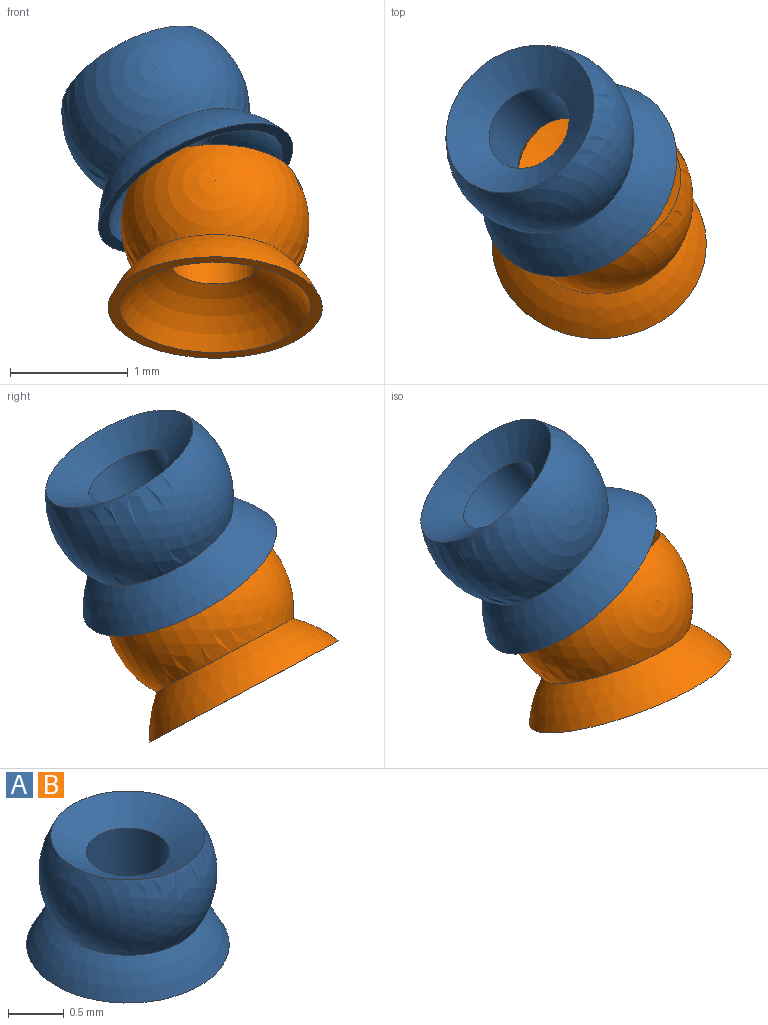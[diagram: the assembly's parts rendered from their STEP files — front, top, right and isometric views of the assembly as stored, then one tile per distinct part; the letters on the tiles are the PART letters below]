
ASSEMBLY  parts=2 mates=1
PART A: 6 faces, bbox 1.8x1.8x1.6 mm
  f0: sphere r=0.9mm, area 2.4mm2, adj f3,f4
  f1: sphere r=0.8mm, area 4.3mm2, adj f2,f5
  f2: sphere r=0.99mm, area 2.2mm2, adj f1,f3
  f3: plane 1.82x1.82mm, normal (0,0,-1), area 0.5mm2, adj f0,f2
  f4: cylinder r=0.38mm len=0.75mm, axis (0,0,-1), area 1.4mm2, adj f0,f5
  f5: cone r=0mm half-angle=60deg, axis (0,0,1), area 1.2mm2, adj f1,f4
PART B: same geometry as A
PLACE A rot(axis=(-0.41,0.03,0.91),101.6deg) t=(1.57,-0.53,1.61)mm
PLACE B rot(axis=(-0.24,0.24,0.94),93.4deg) t=(2.07,-1.04,0.66)mm
MATE ball A.f4 <-> B.f4  axis (-0.42,0.43,0.8) through (2.07,-1.04,0.66)mm
